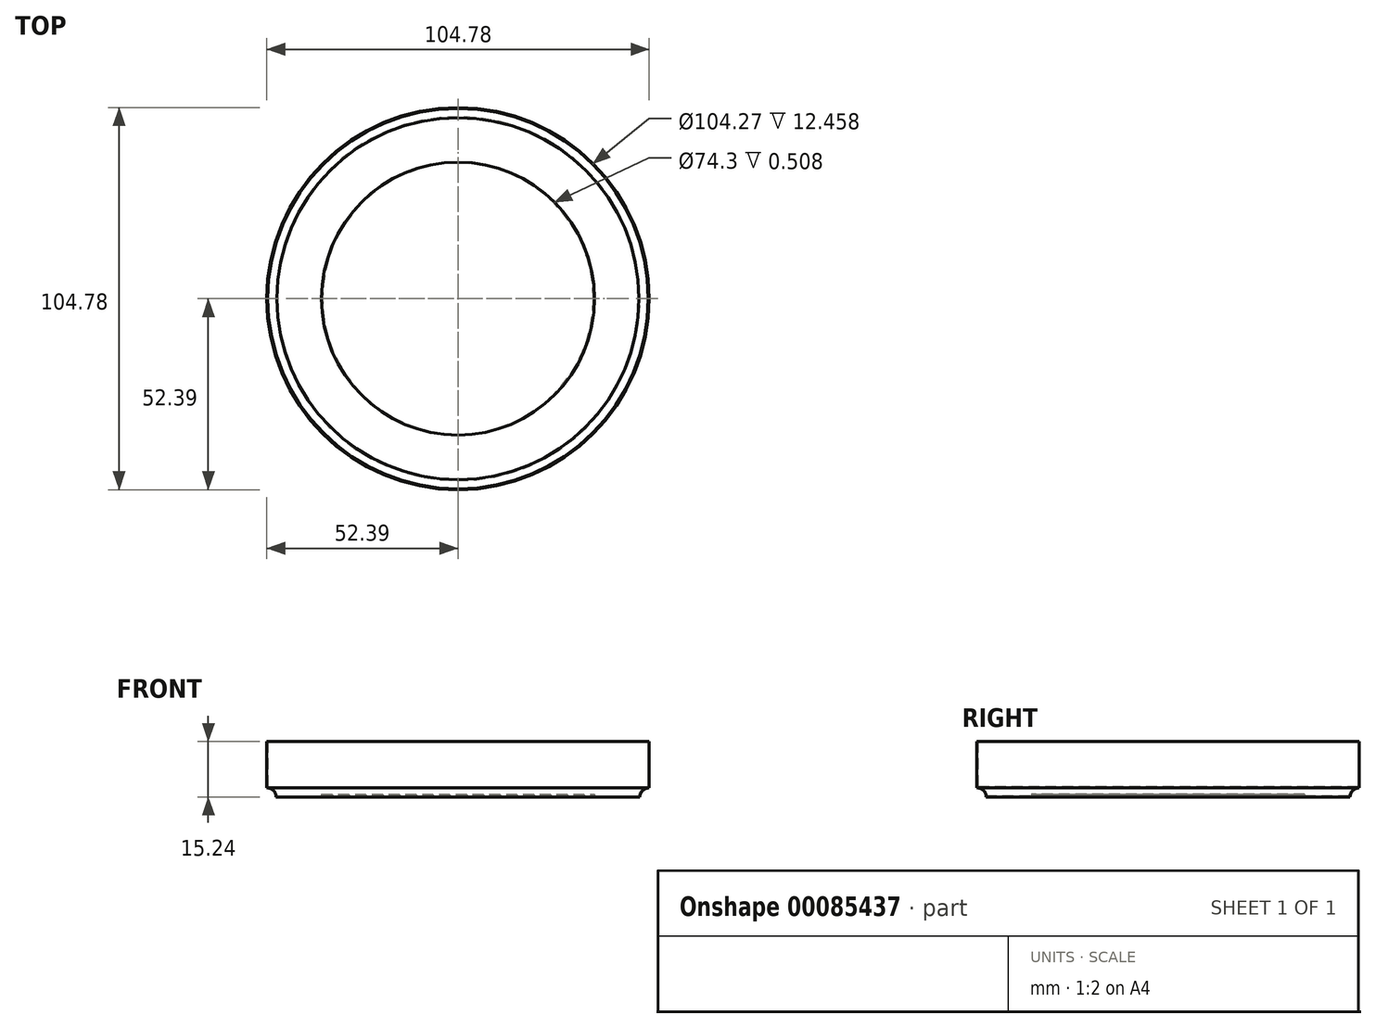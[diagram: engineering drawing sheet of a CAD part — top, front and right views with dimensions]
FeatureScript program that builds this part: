
annotation { "Feature Type Name" : "Feature", "Feature Type Description" : "" }
export const myFeature = defineFeature(function(context is Context, id is Id, definition is map)
    precondition{}
    {
        {
            var Q0;
            Q0=qCreatedBy(makeId("Front.planeOp"),FACE);
            var sketch = newSketch(context, id + "F0", { "sketchPlane" : qUnion([Q0])});
            skLineSegment(sketch, "E0", {"start": v(0, 0) * mm, "end": v(0, 96.22) * mm, "construction": true});
            skLineSegment(sketch, "E1", {"start": v(37.15, 0) * mm, "end": v(49.85, 0) * mm});
            skLineSegment(sketch, "E2", {"start": v(52.39, 2.54) * mm, "end": v(52.39, 15.24) * mm});
            skLineSegment(sketch, "E3", {"start": v(37.15, 0) * mm, "end": v(37.15, 0.5) * mm});
            skLineSegment(sketch, "E4", {"start": v(37.15, 0.5) * mm, "end": v(0, 0.5) * mm});
            skArc(sketch, "E5", {"start": v(52.39, 2.54) * mm, "mid": v(50.6, 1.8) * mm, "end": v(49.85, 0) * mm});
            skLineSegment(sketch, "E6.0", {"start": v(37.4, 0.76) * mm, "end": v(0, 0.76) * mm});
            skLineSegment(sketch, "E6.1", {"start": v(52.13, 2.78) * mm, "end": v(52.13, 15.24) * mm});
            skArc(sketch, "E6.2", {"start": v(52.13, 2.78) * mm, "mid": v(50.41, 1.98) * mm, "end": v(49.6, 0.25) * mm});
            skLineSegment(sketch, "E6.3", {"start": v(37.4, 0.25) * mm, "end": v(49.6, 0.25) * mm});
            skLineSegment(sketch, "E6.4", {"start": v(37.4, 0.25) * mm, "end": v(37.4, 0.76) * mm});
            skLineSegment(sketch, "E7", {"start": v(52.13, 15.24) * mm, "end": v(52.39, 15.24) * mm});
            skLineSegment(sketch, "E8", {"start": v(0, 0.5) * mm, "end": v(0, 0.76) * mm});
            skSolve(sketch);
        }
        {
            var Q0;
            Q0 = qSketchRegion(id + "F0", true);
            var Q1;
            Q1=sQuery(id+"F0.wireOp",EDGE,"E0");
            revolve(context, id + "F1", {"entities" : qUnion([Q0]), "axis" : qUnion([Q1]), "revolveType" : RevolveType.FULL});
        }
    });
